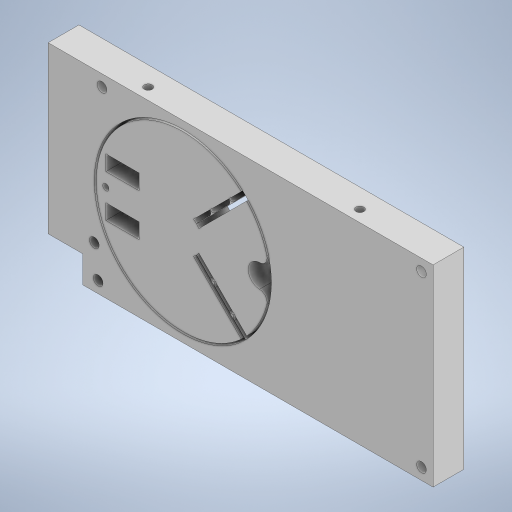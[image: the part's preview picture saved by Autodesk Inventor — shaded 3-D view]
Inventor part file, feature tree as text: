
AUTODESK INVENTOR PART (.ipt)
format: ipt  version: 2023 (Build 270158000, 158)  size: 409,088 bytes
history: native  units: mm
features: extrude x8, sketch x8, reference x6, other x5, fillet x1
ambient origin geometry x8: Origin, YZ Plane, XZ Plane, XY Plane, X Axis, Y Axis, Z Axis, Center Point
bodies: Solid1 (feature_tree)
feature tree (28):
  extrude  "Extrusion1"  Depth=100.0mm
  extrude  "Extrusion4"  Depth=5.0mm
  fillet  "Fillet2"  Radius=5.0mm
  extrude  "Extrusion5"  Depth=5.0mm
  extrude  "Extrusion6"  Depth=15.0mm
  extrude  "Extrusion7"  Depth=3.5mm
  extrude  "Extrusion8"  Depth=3.5mm
  extrude  "Extrusion9"  Depth=8.0mm TaperAngle=0.0deg
  extrude  "Extrusion10"  Depth=10.0mm
  sketch  "Sketch1"  dims[d0=50.0mm d1=100.0mm]
  sketch  "Sketch4"  dims[d2=5.0mm d3=5.0mm d4=5.0mm]
  sketch  "Sketch5"  dims[d5=5.0mm d6=5.0mm]
  sketch  "Sketch6"  dims[d7=15.0mm d8=15.0mm]
  reference  "Reference4"
  reference  "Reference5"
  sketch  "Sketch7"  dims[d9=5.0mm d10=3.5mm]
  reference  "Reference6"
  reference  "Reference7"
  reference  "Reference9"
  reference  "Reference10"
  sketch  "Sketch8"  dims[d11=3.5mm d12=3.5mm]
  sketch  "Sketch9"  dims[d13=3.5mm d14=8.0mm d15=0.0mm]
  sketch  "Sketch10"  dims[d22=15.0mm d23=40.0mm d24=20.0mm d25=45.0mm d26=1.6mm d27=6.0mm d28=45.0deg d29=45.0deg d30=46.0mm d31=25.0mm d32=25.0mm d33=25.0mm d34=10.0mm d35=1.0mm d36=1.0mm d37=0.1mm d38=0.05mm d39=0.1mm d40=0.05mm d41=1.0mm d42=1.0mm d43=8.0mm d44=0.0mm d46=2.0mm d47=15.0mm d48=1.5mm d49=9.0mm d50=0.0mm d51=7.0mm d52=1.6mm d53=1.6mm d54=8.0mm d55=0.0mm d56=2.5mm d57=2.5mm d58=2.5mm d59=2.5mm d60=2.5mm d61=8.0mm d62=0.0mm d63=2.5mm d64=3.0mm d65=4.0mm d66=8.0mm d67=0.0mm d68=2.05mm d69=2.05mm d70=2.05mm d71=2.05mm d72=8.0mm d73=0.0mm d74=23.0mm d75=23.0mm d76=55.0mm d77=23.0mm d78=55.0mm d79=5.0mm d80=2.0mm d81=5.0mm d82=2.0mm d83=5.0mm d84=2.0mm d85=5.0mm d86=2.0mm d87=3.5mm d88=3.5mm d89=4.0mm d90=4.0mm d91=0.0mm d92=8.61mm d93=10.0mm d94=0.0mm]
  other  "<userpath>\ClawdDrive\Objet3D\IminaProbe\V3Roue\RoueV3.iam"
  other  "RoueV3.iam"
  other  "CapacitiveSensor:1"
  other  "RoueV3PartB:1"
  other  "RoueV3PartC:1"
